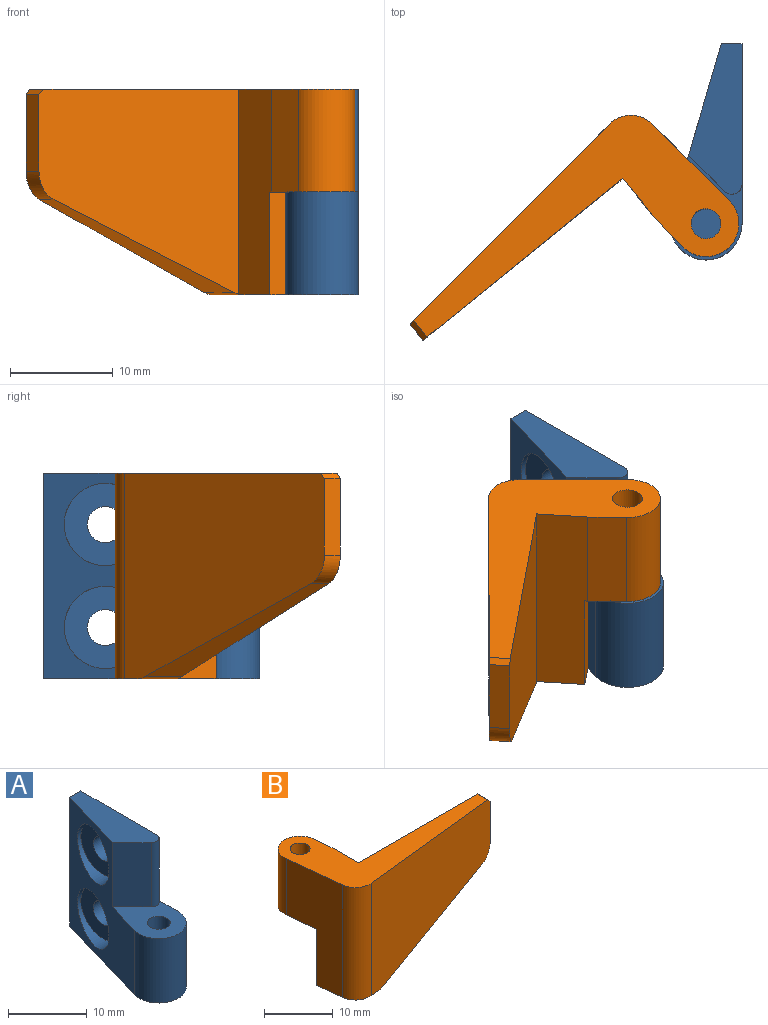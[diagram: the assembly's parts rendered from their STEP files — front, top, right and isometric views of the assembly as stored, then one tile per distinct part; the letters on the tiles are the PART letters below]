
ASSEMBLY  parts=2 mates=1
PART A: 17 faces, bbox 7.5x21.5x20.5 mm
  f0: cylinder r=4mm len=8mm, axis (1,0,0), area 45.4mm2, adj f3,f15
  f1: cylinder r=4mm len=8mm, axis (1,0,0), area 45.4mm2, adj f3,f13
  f2: plane 20x17.5mm, normal (1,0,0), area 292.1mm2, adj f4,f5,f6,f7,f11,f12,f14,f16
  f3: plane 20.49x17.01mm, normal (-0.96,0.28,0), area 180.5mm2, adj f0,f1,f4,f5,f6,f7,f10,f11
  f4: cylinder r=3.5mm len=10mm, axis (0,0,1), area 120mm2, adj f2,f3,f6,f7
  f5: plane 20x2mm, normal (0,1,0), area 40mm2, adj f2,f3,f6,f11
  f6: plane 21x7mm, normal (0,0,-1), area 99.2mm2, adj f2,f3,f4,f5
  f7: plane 10.14x7mm, normal (0,0,1), area 41.3mm2, adj f2,f3,f4,f8,f10,f16
  f8: cylinder r=1.45mm len=9mm, axis (0,0,1), area 82mm2, adj f7,f9
  f9: plane 2.9x2.9mm, normal (0,0,1), area 6.6mm2, adj f8
  f10: plane 10x3.49mm, normal (-0.71,-0.71,0), area 49.3mm2, adj f3,f7,f11,f16
  f11: plane 14.64x5.19mm, normal (0,0,1), area 51.3mm2, adj f2,f3,f5,f10,f16
  f12: cylinder r=1.75mm len=3.5mm, axis (1,0,0), area 22mm2, adj f2,f13
  f13: plane 8x8mm, normal (-1,0,0), area 40.6mm2, adj f1,f12
  f14: cylinder r=1.75mm len=3.5mm, axis (1,0,0), area 22mm2, adj f2,f15
  f15: plane 8x8mm, normal (-1,0,0), area 40.6mm2, adj f0,f14
  f16: cylinder r=1mm len=10mm, axis (0,0,1), area 23.6mm2, adj f2,f7,f10,f11
PART B: 18 faces, bbox 31.7x16.6x20 mm
  f0: plane 20x10.42mm, normal (-0.99,-0.11,0), area 152.4mm2, adj f1,f8,f9,f11,f14,f17
  f1: cylinder r=3.2mm len=10mm, axis (0,0,-1), area 101.3mm2, adj f0,f7,f8,f9
  f2: plane 27.26x20mm, normal (0.11,-0.99,0), area 421.7mm2, adj f3,f8,f11,f12,f13,f14,f15,f16
  f3: plane 7.47x2mm, normal (1,0,0), area 14.9mm2, adj f2,f4,f15,f16
  f4: plane 25x19.94mm, normal (0,1,0), area 374.1mm2, adj f3,f5,f8,f12,f13,f15,f16
  f5: plane 19.94x5mm, normal (1,0,0), area 96.7mm2, adj f4,f7,f8,f9,f10,f13
  f6: cylinder r=1.45mm len=10mm, axis (0,0,-1), area 91.1mm2, adj f8,f9
  f7: plane 10x3.76mm, normal (1,0.08,0), area 37.8mm2, adj f1,f5,f8,f9
  f8: plane 31.2x16.64mm, normal (0,0,1), area 170.3mm2, adj f0,f1,f2,f4,f5,f6,f7,f14
  f9: plane 9.23x6.7mm, normal (0,0,-1), area 37.6mm2, adj f0,f1,f5,f6,f7,f10,f17
  f10: plane 10x2.84mm, normal (0,1,0), area 28.4mm2, adj f5,f9,f11,f13,f17
  f11: plane 9.64x5.49mm, normal (0,0,-1), area 44.7mm2, adj f0,f2,f10,f13,f14,f17
  f12: plane 22.58x9.03mm, normal (0.37,0,-0.93), area 83mm2, adj f2,f4,f13,f15
  f13: cylinder r=3mm len=9.44mm, axis (0,-1,0), area 8.1mm2, adj f2,f4,f5,f10,f11,f12
  f14: cylinder r=3mm len=20mm, axis (0,0,-1), area 94.2mm2, adj f0,f2,f8,f11
  f15: cylinder r=3mm len=2.79mm, axis (0,1,0), area 7.4mm2, adj f2,f3,f4,f12
  f16: plane 2.05x0.5mm, normal (0.71,0,0.71), area 1.4mm2, adj f2,f3,f4,f8
  f17: plane 10x3.23mm, normal (-0.57,0.82,0), area 39.2mm2, adj f0,f9,f10,f11
PLACE A at identity fixed
PLACE B rot(axis=(0,0,-1),141deg) t=(138.47,-455.97,0)mm
MATE revolute B.f1 <-> A.f4  axis (0,0,-1) through (-11.5,-252.5,973.8)mm
